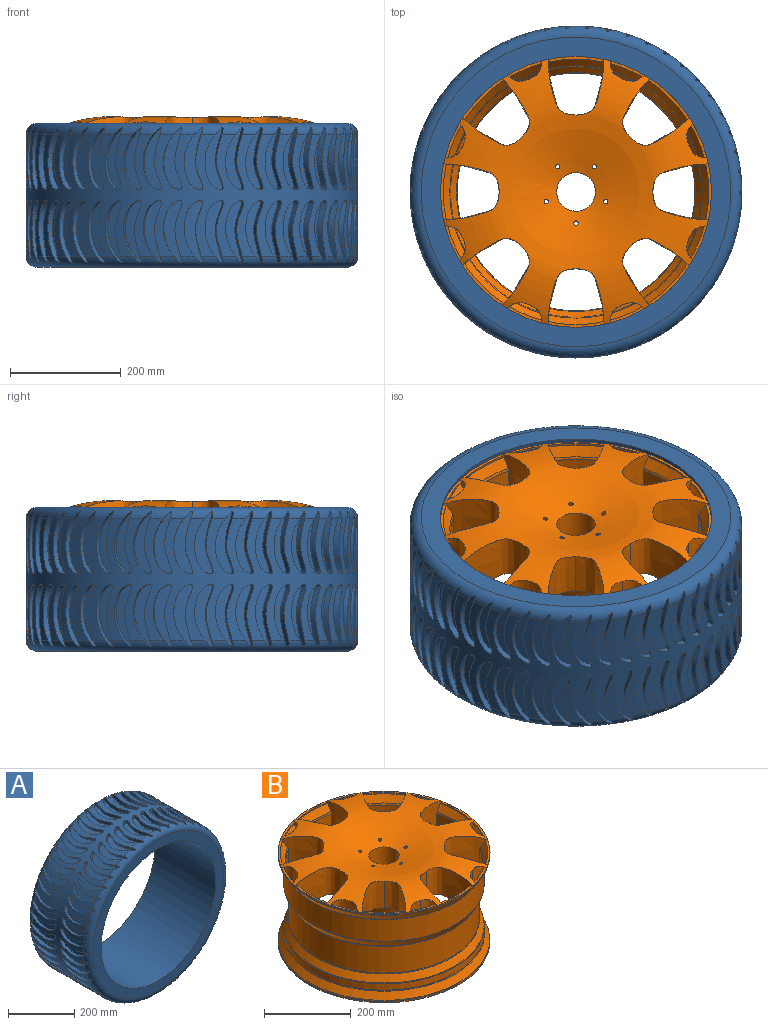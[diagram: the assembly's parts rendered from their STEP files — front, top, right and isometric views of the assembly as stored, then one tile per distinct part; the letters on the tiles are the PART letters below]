
ASSEMBLY  parts=2 mates=1
PART A: 208 faces, bbox 649.5x260x649.5 mm
  f0: cylinder r=300mm len=600mm, axis (0,1,0), area 178551.5mm2, adj f5,f7,f9,f11,f13,f15,f17,f19
  f1: plane 560x560mm, normal (0,1,0), area 57726.8mm2, adj f3,f206
  f2: plane 560x560mm, normal (0,-1,0), area 57726.8mm2, adj f3,f204
  f3: cylinder r=245mm len=490mm, axis (0,-1,0), area 400238.9mm2, adj f1,f2
  f4: plane 115.04x28.53mm, normal (0.64,0,0.77), area 2066.3mm2, adj f5
  f5: extruded ~112.28x33.37mm, area 2877.2mm2, adj f0,f4,f204
  f6: plane 115.04x35.82mm, normal (0.99,0,0.13), area 2066.3mm2, adj f7
  f7: extruded ~112.28x34.63mm, area 2877.2mm2, adj f0,f6,f204
  f8: plane 115.04x27.16mm, normal (0.73,0,-0.68), area 2066.3mm2, adj f9
  f9: extruded ~112.28x32.55mm, area 2877.2mm2, adj f0,f8,f204
  f10: plane 115.04x30.96mm, normal (0.54,0,-0.84), area 2066.3mm2, adj f11
  f11: extruded ~112.28x34.62mm, area 2877.2mm2, adj f0,f10,f204
  f12: plane 115.04x28.53mm, normal (0.64,0,-0.77), area 2066.3mm2, adj f13
  f13: extruded ~112.28x33.37mm, area 2877.2mm2, adj f0,f12,f204
  f14: plane 115.04x33.77mm, normal (0.93,0,-0.37), area 2066.3mm2, adj f15
  f15: extruded ~112.28x35.46mm, area 2877.2mm2, adj f0,f14,f204
  f16: plane 115.04x35.04mm, normal (0.97,0,-0.25), area 2066.3mm2, adj f17
  f17: extruded ~112.28x35.32mm, area 2877.2mm2, adj f0,f16,f204
  f18: plane 115.04x29.79mm, normal (0.81,0,-0.59), area 2066.3mm2, adj f19
  f19: extruded ~112.28x34.06mm, area 2877.2mm2, adj f0,f18,f204
  f20: plane 115.04x32.01mm, normal (0.88,0,-0.48), area 2066.3mm2, adj f21
  f21: extruded ~112.28x35.04mm, area 2877.2mm2, adj f0,f20,f204
  f22: plane 115.04x36.01mm, normal (0.06,0,-1), area 2066.3mm2, adj f23
  f23: extruded ~112.28x34.08mm, area 2877.2mm2, adj f0,f22,f204
  f24: plane 115.04x35.49mm, normal (0.19,0,-0.98), area 2066.3mm2, adj f25
  f25: extruded ~112.28x35.04mm, area 2877.2mm2, adj f0,f24,f204
  f26: plane 115.04x32.95mm, normal (0.43,0,-0.9), area 2066.3mm2, adj f27
  f27: extruded ~112.28x35.32mm, area 2877.2mm2, adj f0,f26,f204
  f28: plane 115.04x34.47mm, normal (0.31,0,-0.95), area 2066.3mm2, adj f29
  f29: extruded ~112.28x35.46mm, area 2877.2mm2, adj f0,f28,f204
  f30: plane 115.04x34.47mm, normal (-0.31,0,-0.95), area 2066.3mm2, adj f31
  f31: extruded ~112.28x35.46mm, area 2877.2mm2, adj f0,f30,f204
  f32: plane 115.04x32.95mm, normal (-0.43,0,-0.9), area 2066.3mm2, adj f33
  f33: extruded ~112.28x35.32mm, area 2877.2mm2, adj f0,f32,f204
  f34: plane 115.04x35.49mm, normal (-0.19,0,-0.98), area 2066.3mm2, adj f35
  f35: extruded ~112.28x35.04mm, area 2877.2mm2, adj f0,f34,f204
  f36: plane 115.04x36.01mm, normal (-0.06,0,-1), area 2066.3mm2, adj f37
  f37: extruded ~112.28x34.08mm, area 2877.2mm2, adj f0,f36,f204
  f38: plane 115.04x35.82mm, normal (0.99,0,-0.13), area 2066.3mm2, adj f39
  f39: extruded ~112.28x34.63mm, area 2877.2mm2, adj f0,f38,f204
  f40: plane 115.04x34.47mm, normal (-0.31,0,0.95), area 2066.3mm2, adj f41
  f41: extruded ~112.28x35.46mm, area 2877.2mm2, adj f0,f40,f204
  f42: plane 115.04x35.49mm, normal (-0.19,0,0.98), area 2066.3mm2, adj f43
  f43: extruded ~112.28x35.04mm, area 2877.2mm2, adj f0,f42,f204
  f44: plane 115.04x30.96mm, normal (-0.54,0,0.84), area 2066.3mm2, adj f45
  f45: extruded ~112.28x34.62mm, area 2877.2mm2, adj f0,f44,f204
  f46: plane 115.04x32.95mm, normal (-0.43,0,0.9), area 2066.3mm2, adj f47
  f47: extruded ~112.28x35.32mm, area 2877.2mm2, adj f0,f46,f204
  f48: plane 115.04x36.01mm, normal (-0.06,0,1), area 2066.3mm2, adj f49
  f49: extruded ~112.28x34.08mm, area 2877.2mm2, adj f0,f48,f204
  f50: plane 115.04x36.01mm, normal (0.06,0,1), area 2066.3mm2, adj f51
  f51: extruded ~112.28x34.08mm, area 2877.2mm2, adj f0,f50,f204
  f52: plane 115.04x34.47mm, normal (0.31,0,0.95), area 2066.3mm2, adj f53
  f53: extruded ~112.28x35.46mm, area 2877.2mm2, adj f0,f52,f204
  f54: plane 115.04x35.49mm, normal (0.19,0,0.98), area 2066.3mm2, adj f55
  f55: extruded ~112.28x35.04mm, area 2877.2mm2, adj f0,f54,f204
  f56: plane 115.04x27.16mm, normal (0.73,0,0.68), area 2066.3mm2, adj f57
  f57: extruded ~112.28x32.55mm, area 2877.2mm2, adj f0,f56,f204
  f58: plane 115.04x29.79mm, normal (0.81,0,0.59), area 2066.3mm2, adj f59
  f59: extruded ~112.28x34.06mm, area 2877.2mm2, adj f0,f58,f204
  f60: plane 115.04x30.96mm, normal (0.54,0,0.84), area 2066.3mm2, adj f61
  f61: extruded ~112.28x34.62mm, area 2877.2mm2, adj f0,f60,f204
  f62: plane 115.04x36.08mm, normal (1,0,0), area 2066.3mm2, adj f63
  f63: extruded ~112.28x33.39mm, area 2877.2mm2, adj f0,f62,f204
  f64: plane 115.04x32.95mm, normal (0.43,0,0.9), area 2066.3mm2, adj f65
  f65: extruded ~112.28x35.32mm, area 2877.2mm2, adj f0,f64,f204
  f66: plane 115.04x35.04mm, normal (0.97,0,0.25), area 2066.3mm2, adj f67
  f67: extruded ~112.28x35.32mm, area 2877.2mm2, adj f0,f66,f204
  f68: plane 115.04x32.01mm, normal (0.88,0,0.48), area 2066.3mm2, adj f69
  f69: extruded ~112.28x35.04mm, area 2877.2mm2, adj f0,f68,f204
  f70: plane 115.04x33.77mm, normal (0.93,0,0.37), area 2066.3mm2, adj f71
  f71: extruded ~112.28x35.46mm, area 2877.2mm2, adj f0,f70,f204
  f72: plane 115.04x35.04mm, normal (-0.97,0,0.25), area 2066.3mm2, adj f73
  f73: extruded ~112.28x35.32mm, area 2877.2mm2, adj f0,f72,f204
  f74: plane 115.04x33.77mm, normal (-0.93,0,0.37), area 2066.3mm2, adj f75
  f75: extruded ~112.28x35.46mm, area 2877.2mm2, adj f0,f74,f204
  f76: plane 115.04x35.82mm, normal (-0.99,0,0.13), area 2066.3mm2, adj f77
  f77: extruded ~112.28x34.63mm, area 2877.2mm2, adj f0,f76,f204
  f78: plane 115.04x36.08mm, normal (-1,0,0), area 2066.3mm2, adj f79
  f79: extruded ~112.28x33.39mm, area 2876.8mm2, adj f0,f78,f204,f205
  f80: plane 115.04x27.16mm, normal (-0.73,0,0.68), area 2066.3mm2, adj f81
  f81: extruded ~112.28x32.55mm, area 2877.2mm2, adj f0,f80,f204
  f82: plane 115.04x28.53mm, normal (-0.64,0,0.77), area 2066.3mm2, adj f83
  f83: extruded ~112.28x33.37mm, area 2877.2mm2, adj f0,f82,f204
  f84: plane 115.04x32.01mm, normal (-0.88,0,0.48), area 2066.3mm2, adj f85
  f85: extruded ~112.28x35.04mm, area 2877.2mm2, adj f0,f84,f204
  f86: plane 115.04x29.79mm, normal (-0.81,0,0.59), area 2066.3mm2, adj f87
  f87: extruded ~112.28x34.06mm, area 2877.2mm2, adj f0,f86,f204
  f88: plane 115.04x27.16mm, normal (-0.73,0,-0.68), area 2066.3mm2, adj f89
  f89: extruded ~112.28x32.55mm, area 2877.2mm2, adj f0,f88,f204
  f90: plane 115.04x29.79mm, normal (-0.81,0,-0.59), area 2066.3mm2, adj f91
  f91: extruded ~112.28x34.06mm, area 2877.2mm2, adj f0,f90,f204
  f92: plane 115.04x30.96mm, normal (-0.54,0,-0.84), area 2066.3mm2, adj f93
  f93: extruded ~112.28x34.62mm, area 2877.2mm2, adj f0,f92,f204
  f94: plane 115.04x28.53mm, normal (-0.64,0,-0.77), area 2066.3mm2, adj f95
  f95: extruded ~112.28x33.37mm, area 2877.2mm2, adj f0,f94,f204
  f96: plane 115.04x35.04mm, normal (-0.97,0,-0.25), area 2066.3mm2, adj f97
  f97: extruded ~112.28x35.32mm, area 2877.2mm2, adj f0,f96,f204
  f98: plane 115.04x35.82mm, normal (-0.99,0,-0.13), area 2066.3mm2, adj f99
  f99: extruded ~112.28x34.63mm, area 2877.2mm2, adj f0,f98,f204
  f100: plane 115.04x32.01mm, normal (-0.88,0,-0.48), area 2066.3mm2, adj f101
  f101: extruded ~112.28x35.04mm, area 2877.2mm2, adj f0,f100,f204
  f102: plane 115.04x33.77mm, normal (-0.93,0,-0.37), area 2066.3mm2, adj f103
  f103: extruded ~112.28x35.46mm, area 2877.2mm2, adj f0,f102,f204
  f104: plane 115.04x28.53mm, normal (0.64,0,0.77), area 2066.4mm2, adj f105
  f105: extruded ~112.28x33.37mm, area 2877.2mm2, adj f0,f104,f206
  f106: plane 115.04x35.5mm, normal (0.19,0,-0.98), area 2066.4mm2, adj f107
  f107: extruded ~112.28x35.04mm, area 2877.2mm2, adj f0,f106,f206
  f108: plane 115.04x34.47mm, normal (0.31,0,-0.95), area 2066.4mm2, adj f109
  f109: extruded ~112.28x35.46mm, area 2877.2mm2, adj f0,f108,f206
  f110: plane 115.04x30.96mm, normal (0.54,0,-0.84), area 2066.4mm2, adj f111
  f111: extruded ~112.28x34.62mm, area 2877.2mm2, adj f0,f110,f206
  f112: plane 115.04x35.04mm, normal (0.97,0,-0.25), area 2066.4mm2, adj f113
  f113: extruded ~112.28x35.32mm, area 2877.2mm2, adj f0,f112,f206
  f114: plane 115.04x35.04mm, normal (0.97,0,0.25), area 2066.4mm2, adj f115
  f115: extruded ~112.28x35.32mm, area 2877.2mm2, adj f0,f114,f206
  f116: plane 115.04x33.77mm, normal (0.93,0,-0.37), area 2066.4mm2, adj f117
  f117: extruded ~112.28x35.46mm, area 2877.2mm2, adj f0,f116,f206
  f118: plane 115.04x35.82mm, normal (0.99,0,-0.13), area 2066.4mm2, adj f119
  f119: extruded ~112.28x34.63mm, area 2877.2mm2, adj f0,f118,f206
  f120: plane 115.04x32.95mm, normal (0.43,0,-0.9), area 2066.4mm2, adj f121
  f121: extruded ~112.28x35.32mm, area 2877.2mm2, adj f0,f120,f206
  f122: plane 115.04x28.53mm, normal (0.64,0,-0.77), area 2066.4mm2, adj f123
  f123: extruded ~112.28x33.37mm, area 2877.2mm2, adj f0,f122,f206
  f124: plane 115.04x28.53mm, normal (-0.64,0,-0.77), area 2066.4mm2, adj f125
  f125: extruded ~112.28x33.37mm, area 2877.2mm2, adj f0,f124,f206
  f126: plane 115.04x32.95mm, normal (-0.43,0,-0.9), area 2066.4mm2, adj f127
  f127: extruded ~112.28x35.32mm, area 2877.2mm2, adj f0,f126,f206
  f128: plane 115.04x30.96mm, normal (-0.54,0,-0.84), area 2066.4mm2, adj f129
  f129: extruded ~112.28x34.62mm, area 2877.2mm2, adj f0,f128,f206
  f130: plane 115.04x36.08mm, normal (1,0,0), area 2066.4mm2, adj f131
  f131: extruded ~112.28x33.39mm, area 2877.2mm2, adj f0,f130,f206
  f132: plane 115.04x32.01mm, normal (0.88,0,-0.48), area 2066.4mm2, adj f133
  f133: extruded ~112.28x35.04mm, area 2877.2mm2, adj f0,f132,f206
  f134: plane 115.04x27.16mm, normal (0.73,0,-0.68), area 2066.4mm2, adj f135
  f135: extruded ~112.28x32.55mm, area 2877.2mm2, adj f0,f134,f206
  f136: plane 115.04x29.8mm, normal (0.81,0,-0.59), area 2066.4mm2, adj f137
  f137: extruded ~112.28x34.06mm, area 2877.2mm2, adj f0,f136,f206
  f138: plane 115.04x35.82mm, normal (0.99,0,0.13), area 2066.4mm2, adj f139
  f139: extruded ~112.28x34.63mm, area 2877.2mm2, adj f0,f138,f206
  f140: plane 115.04x30.96mm, normal (-0.54,0,0.84), area 2066.4mm2, adj f141
  f141: extruded ~112.28x34.62mm, area 2877.2mm2, adj f0,f140,f206
  f142: plane 115.04x32.95mm, normal (-0.43,0,0.9), area 2066.4mm2, adj f143
  f143: extruded ~112.28x35.32mm, area 2877.2mm2, adj f0,f142,f206
  f144: plane 115.04x27.16mm, normal (-0.73,0,0.68), area 2066.4mm2, adj f145
  f145: extruded ~112.28x32.55mm, area 2877.2mm2, adj f0,f144,f206
  f146: plane 115.04x28.53mm, normal (-0.64,0,0.77), area 2066.4mm2, adj f147
  f147: extruded ~112.28x33.37mm, area 2877.2mm2, adj f0,f146,f206
  f148: plane 115.04x36.01mm, normal (0.06,0,1), area 2066.4mm2, adj f149
  f149: extruded ~112.28x34.08mm, area 2877.2mm2, adj f0,f148,f206
  f150: plane 115.04x35.5mm, normal (0.19,0,0.98), area 2066.4mm2, adj f151
  f151: extruded ~112.28x35.04mm, area 2877.2mm2, adj f0,f150,f206
  f152: plane 115.04x32.95mm, normal (0.43,0,0.9), area 2066.4mm2, adj f153
  f153: extruded ~112.28x35.32mm, area 2877.2mm2, adj f0,f152,f206
  f154: plane 115.04x34.47mm, normal (0.31,0,0.95), area 2066.4mm2, adj f155
  f155: extruded ~112.28x35.46mm, area 2877.2mm2, adj f0,f154,f206
  f156: plane 115.04x29.8mm, normal (0.81,0,0.59), area 2066.4mm2, adj f157
  f157: extruded ~112.28x34.06mm, area 2877.2mm2, adj f0,f156,f206
  f158: plane 115.04x32.01mm, normal (0.88,0,0.48), area 2066.4mm2, adj f159
  f159: extruded ~112.28x35.04mm, area 2877.2mm2, adj f0,f158,f206
  f160: plane 115.04x27.16mm, normal (0.73,0,0.68), area 2066.4mm2, adj f161
  f161: extruded ~112.28x32.55mm, area 2877.2mm2, adj f0,f160,f206
  f162: plane 115.04x30.96mm, normal (0.54,0,0.84), area 2066.4mm2, adj f163
  f163: extruded ~112.28x34.62mm, area 2877.2mm2, adj f0,f162,f206
  f164: plane 115.04x36.01mm, normal (-0.06,0,1), area 2066.4mm2, adj f165
  f165: extruded ~112.28x34.08mm, area 2877.2mm2, adj f0,f164,f206
  f166: plane 115.04x35.5mm, normal (-0.19,0,0.98), area 2066.4mm2, adj f167
  f167: extruded ~112.28x35.04mm, area 2877.2mm2, adj f0,f166,f206
  f168: plane 115.04x34.47mm, normal (-0.31,0,0.95), area 2066.4mm2, adj f169
  f169: extruded ~112.28x35.46mm, area 2877.2mm2, adj f0,f168,f206
  f170: plane 115.04x33.77mm, normal (0.93,0,0.37), area 2066.4mm2, adj f171
  f171: extruded ~112.28x35.46mm, area 2877.2mm2, adj f0,f170,f206
  f172: plane 115.04x35.5mm, normal (-0.19,0,-0.98), area 2066.4mm2, adj f173
  f173: extruded ~112.28x35.04mm, area 2877.2mm2, adj f0,f172,f206
  f174: plane 115.04x34.47mm, normal (-0.31,0,-0.95), area 2066.4mm2, adj f175
  f175: extruded ~112.28x35.46mm, area 2877.2mm2, adj f0,f174,f206
  f176: plane 115.04x36.01mm, normal (-0.06,0,-1), area 2066.4mm2, adj f177
  f177: extruded ~112.28x34.08mm, area 2877.2mm2, adj f0,f176,f206
  f178: plane 115.04x36.01mm, normal (0.06,0,-1), area 2066.4mm2, adj f179
  f179: extruded ~112.28x34.08mm, area 2877.2mm2, adj f0,f178,f206
  f180: plane 115.04x32.01mm, normal (-0.88,0,-0.48), area 2066.4mm2, adj f181
  f181: extruded ~112.28x35.04mm, area 2877.2mm2, adj f0,f180,f206
  f182: plane 115.04x33.77mm, normal (-0.93,0,-0.37), area 2066.4mm2, adj f183
  f183: extruded ~112.28x35.46mm, area 2877.2mm2, adj f0,f182,f206
  f184: plane 115.04x27.16mm, normal (-0.73,0,-0.68), area 2066.4mm2, adj f185
  f185: extruded ~112.28x32.55mm, area 2877.2mm2, adj f0,f184,f206
  f186: plane 115.04x29.8mm, normal (-0.81,0,-0.59), area 2066.4mm2, adj f187
  f187: extruded ~112.28x34.06mm, area 2877.2mm2, adj f0,f186,f206
  f188: plane 115.04x33.77mm, normal (-0.93,0,0.37), area 2066.4mm2, adj f189
  f189: extruded ~112.28x35.46mm, area 2877.2mm2, adj f0,f188,f206
  f190: plane 115.04x35.04mm, normal (-0.97,0,0.25), area 2066.4mm2, adj f191
  f191: extruded ~112.28x35.32mm, area 2877.2mm2, adj f0,f190,f206
  f192: plane 115.04x29.8mm, normal (-0.81,0,0.59), area 2066.4mm2, adj f193
  f193: extruded ~112.28x34.06mm, area 2877.2mm2, adj f0,f192,f206
  f194: plane 115.04x32.01mm, normal (-0.88,0,0.48), area 2066.4mm2, adj f195
  f195: extruded ~112.28x35.04mm, area 2877.2mm2, adj f0,f194,f206
  f196: plane 115.04x35.82mm, normal (-0.99,0,0.13), area 2066.4mm2, adj f197
  f197: extruded ~112.28x34.63mm, area 2877.2mm2, adj f0,f196,f206
  f198: plane 115.04x36.08mm, normal (-1,0,0), area 2066.4mm2, adj f199
  f199: extruded ~112.28x33.39mm, area 2876.8mm2, adj f0,f198,f206,f207
  f200: plane 115.04x35.04mm, normal (-0.97,0,-0.25), area 2066.4mm2, adj f201
  f201: extruded ~112.28x35.32mm, area 2877.2mm2, adj f0,f200,f206
  f202: plane 115.04x35.82mm, normal (-0.99,0,-0.13), area 2066.4mm2, adj f203
  f203: extruded ~112.28x34.63mm, area 2877.2mm2, adj f0,f202,f206
  f204: torus R=280mm, axis (0,1,0), area 52595.4mm2, adj f0,f2,f5,f7,f9,f11,f13,f15
  f205: torus R=280mm, axis (0,1,0), area 6.9mm2, adj f0,f79,f204
  f206: torus R=280mm, axis (0,1,0), area 52606.5mm2, adj f0,f1,f105,f107,f109,f111,f113,f115
  f207: torus R=280mm, axis (0,1,0), area 6.9mm2, adj f0,f199,f206
PART B: 133 faces, bbox 530.4x530.4x270.1 mm
  f0: cylinder r=4mm len=167.44mm, axis (0,0,-1), area 4178.2mm2, adj f4,f28
  f1: cylinder r=4mm len=167.44mm, axis (0,0,-1), area 4178.2mm2, adj f4,f28
  f2: cylinder r=4mm len=167.44mm, axis (0,0,-1), area 4178.2mm2, adj f4,f28
  f3: cylinder r=4mm len=167.44mm, axis (0,0,-1), area 4178.2mm2, adj f4,f28
  f4: revolved ~490x490mm, area 106451.8mm2, adj f0,f1,f2,f3,f5,f6,f7,f8
  f5: extruded ~95.98x33.16mm, area 2397mm2, adj f4,f22,f29,f45,f61,f62,f77,f92
  f6: extruded ~95.98x39.81mm, area 2397mm2, adj f4,f22,f30,f46,f61,f63,f78,f93
  f7: extruded ~107.05x105.12mm, area 9144.7mm2, adj f4,f22,f31,f47,f61,f64,f79,f94
  f8: extruded ~105.12x100.76mm, area 9144.7mm2, adj f4,f22,f32,f48,f61,f74,f89,f104
  f9: extruded ~105.12x100.76mm, area 9144.7mm2, adj f4,f22,f33,f49,f61,f67,f82,f97
  f10: extruded ~95.98x33.16mm, area 2397mm2, adj f4,f22,f34,f50,f61,f65,f80,f95
  f11: extruded ~95.98x39.81mm, area 2397mm2, adj f4,f22,f35,f51,f61,f66,f81,f96
  f12: extruded ~107.05x105.12mm, area 9144.7mm2, adj f4,f22,f36,f52,f61,f68,f83,f98
  f13: extruded ~105.12x100.76mm, area 9144.7mm2, adj f4,f22,f37,f53,f61,f70,f85,f100
  f14: extruded ~95.98x39.81mm, area 2397mm2, adj f4,f22,f38,f54,f61,f69,f84,f99
  f15: extruded ~107.05x105.12mm, area 9144.7mm2, adj f4,f22,f39,f55,f61,f76,f91,f106
  f16: extruded ~107.05x105.12mm, area 9144.7mm2, adj f4,f22,f40,f56,f61,f72,f87,f102
  f17: extruded ~95.98x39.81mm, area 2397mm2, adj f4,f22,f41,f57,f61,f71,f86,f101
  f18: extruded ~95.98x33.16mm, area 2397mm2, adj f4,f22,f42,f58,f61,f73,f88,f103
  f19: extruded ~95.98x33.16mm, area 2397mm2, adj f4,f22,f43,f59,f61,f75,f90,f105
  f20: extruded ~105.12x100.76mm, area 9144.7mm2, adj f4,f22,f44,f60,f61,f113,f114,f119
  f21: cylinder r=245mm len=490mm, axis (0,0,-1), area 5871.6mm2, adj f4,f27,f45,f46,f47,f48,f49,f50
  f22: revolved ~454x454mm, area 130293mm2, adj f5,f6,f7,f8,f9,f10,f11,f12
  f23: torus R=228mm, axis (0,0,-1), area 3148.5mm2, adj f24,f124
  f24: cylinder r=232mm len=464mm, axis (0,0,-1), area 89949.2mm2, adj f23,f25
  f25: torus R=236mm, axis (0,0,-1), area 3363.9mm2, adj f24,f26
  f26: cone r=244.35mm half-angle=33deg, axis (0,0,1), area 32191.9mm2, adj f25,f27
  f27: torus R=241mm, axis (0,0,-1), area 3545.9mm2, adj f21,f26
  f28: plane 148.24x148.24mm, normal (0,0,-1), area 13159.5mm2, adj f0,f1,f2,f3,f22,f131,f132
  f29: extruded ~95.98x39.81mm, area 2397mm2, adj f4,f5,f22,f45,f61,f62,f77,f92
  f30: extruded ~95.98x33.16mm, area 2397mm2, adj f4,f6,f22,f46,f61,f63,f78,f93
  f31: extruded ~107.05x105.12mm, area 9144.7mm2, adj f4,f7,f22,f47,f61,f64,f79,f94
  f32: extruded ~105.12x100.76mm, area 9144.7mm2, adj f4,f8,f22,f48,f61,f74,f89,f104
  f33: extruded ~105.12x100.76mm, area 9144.7mm2, adj f4,f9,f22,f49,f61,f67,f82,f97
  f34: extruded ~95.98x39.81mm, area 2397mm2, adj f4,f10,f22,f50,f61,f65,f80,f95
  f35: extruded ~95.98x33.16mm, area 2397mm2, adj f4,f11,f22,f51,f61,f66,f81,f96
  f36: extruded ~107.05x105.12mm, area 9144.7mm2, adj f4,f12,f22,f52,f61,f68,f83,f98
  f37: extruded ~105.12x100.76mm, area 9144.7mm2, adj f4,f13,f22,f53,f61,f70,f85,f100
  f38: extruded ~95.98x33.16mm, area 2397mm2, adj f4,f14,f22,f54,f61,f69,f84,f99
  f39: extruded ~107.05x105.12mm, area 9144.7mm2, adj f4,f15,f22,f55,f61,f76,f91,f106
  f40: extruded ~107.05x105.12mm, area 9144.7mm2, adj f4,f16,f22,f56,f61,f72,f87,f102
  f41: extruded ~95.98x33.16mm, area 2397mm2, adj f4,f17,f22,f57,f61,f71,f86,f101
  f42: extruded ~95.98x39.81mm, area 2397mm2, adj f4,f18,f22,f58,f61,f73,f88,f103
  f43: extruded ~95.98x39.81mm, area 2397mm2, adj f4,f19,f22,f59,f61,f75,f90,f105
  f44: extruded ~105.12x100.76mm, area 9144.7mm2, adj f4,f20,f22,f60,f61,f113,f114,f119
  f45: plane 62.96x29.54mm, normal (0,0,1), area 330mm2, adj f5,f21,f29,f77
  f46: plane 62.96x29.54mm, normal (0,0,1), area 330mm2, adj f6,f21,f30,f78
  f47: plane 75.03x75.03mm, normal (0,0,1), area 508.9mm2, adj f7,f21,f31,f79
  f48: plane 101.25x10.36mm, normal (0,0,1), area 508.9mm2, adj f8,f21,f32,f89
  f49: plane 101.25x10.36mm, normal (0,0,1), area 508.9mm2, adj f9,f21,f33,f82
  f50: plane 62.96x29.54mm, normal (0,0,1), area 330mm2, adj f10,f21,f34,f80
  f51: plane 62.96x29.54mm, normal (0,0,1), area 330mm2, adj f11,f21,f35,f81
  f52: plane 75.03x75.03mm, normal (0,0,1), area 508.9mm2, adj f12,f21,f36,f83
  f53: plane 101.25x10.36mm, normal (0,0,1), area 508.9mm2, adj f13,f21,f37,f85
  f54: plane 62.96x29.54mm, normal (0,0,1), area 330mm2, adj f14,f21,f38,f84
  f55: plane 75.03x75.03mm, normal (0,0,1), area 508.9mm2, adj f15,f21,f39,f91
  f56: plane 75.03x75.03mm, normal (0,0,1), area 508.9mm2, adj f16,f21,f40,f87
  f57: plane 62.96x29.54mm, normal (0,0,1), area 330mm2, adj f17,f21,f41,f86
  f58: plane 62.96x29.54mm, normal (0,0,1), area 330mm2, adj f18,f21,f42,f88
  f59: plane 62.96x29.54mm, normal (0,0,1), area 330mm2, adj f19,f21,f43,f90
  f60: plane 101.25x10.36mm, normal (0,0,1), area 508.9mm2, adj f20,f21,f44,f114
  f61: cylinder r=227mm len=454mm, axis (0,0,1), area 70647.6mm2, adj f5,f6,f7,f8,f9,f10,f11,f12
  f62: cone r=227.81mm half-angle=33deg, axis (0,0,1), area 1167.8mm2, adj f5,f29,f77,f92
  f63: cone r=227.81mm half-angle=33deg, axis (0,0,1), area 1167.8mm2, adj f6,f30,f78,f93
  f64: cone r=227.81mm half-angle=33deg, axis (0,0,1), area 2137.5mm2, adj f7,f31,f79,f94
  f65: cone r=227.81mm half-angle=33deg, axis (0,0,1), area 1167.8mm2, adj f10,f34,f80,f95
  f66: cone r=227.81mm half-angle=33deg, axis (0,0,1), area 1167.8mm2, adj f11,f35,f81,f96
  f67: cone r=227.81mm half-angle=33deg, axis (0,0,1), area 2137.5mm2, adj f9,f33,f82,f97
  f68: cone r=227.81mm half-angle=33deg, axis (0,0,1), area 2137.5mm2, adj f12,f36,f83,f98
  f69: cone r=227.81mm half-angle=33deg, axis (0,0,1), area 1167.8mm2, adj f14,f38,f84,f99
  f70: cone r=227.81mm half-angle=33deg, axis (0,0,1), area 2137.5mm2, adj f13,f37,f85,f100
  f71: cone r=227.81mm half-angle=33deg, axis (0,0,1), area 1167.8mm2, adj f17,f41,f86,f101
  f72: cone r=227.81mm half-angle=33deg, axis (0,0,1), area 2137.5mm2, adj f16,f40,f87,f102
  f73: cone r=227.81mm half-angle=33deg, axis (0,0,1), area 1167.8mm2, adj f18,f42,f88,f103
  f74: cone r=227.81mm half-angle=33deg, axis (0,0,1), area 2137.5mm2, adj f8,f32,f89,f104
  f75: cone r=227.81mm half-angle=33deg, axis (0,0,1), area 1167.8mm2, adj f19,f43,f90,f105
  f76: cone r=227.81mm half-angle=33deg, axis (0,0,1), area 2137.5mm2, adj f15,f39,f91,f106
  f77: cylinder r=240mm len=58.53mm, axis (0,0,1), area 223.5mm2, adj f5,f29,f45,f62
  f78: cylinder r=240mm len=58.53mm, axis (0,0,1), area 223.5mm2, adj f6,f30,f46,f63
  f79: cylinder r=240mm len=71.29mm, axis (0,0,1), area 357.3mm2, adj f7,f31,f47,f64
  f80: cylinder r=240mm len=58.53mm, axis (0,0,1), area 223.5mm2, adj f10,f34,f50,f65
  f81: cylinder r=240mm len=58.53mm, axis (0,0,1), area 223.5mm2, adj f11,f35,f51,f66
  f82: cylinder r=240mm len=100.82mm, axis (0,0,1), area 357.3mm2, adj f9,f33,f49,f67
  f83: cylinder r=240mm len=71.29mm, axis (0,0,1), area 357.3mm2, adj f12,f36,f52,f68
  f84: cylinder r=240mm len=58.53mm, axis (0,0,1), area 223.5mm2, adj f14,f38,f54,f69
  f85: cylinder r=240mm len=100.82mm, axis (0,0,1), area 357.3mm2, adj f13,f37,f53,f70
  f86: cylinder r=240mm len=58.53mm, axis (0,0,1), area 223.5mm2, adj f17,f41,f57,f71
  f87: cylinder r=240mm len=71.29mm, axis (0,0,1), area 357.3mm2, adj f16,f40,f56,f72
  f88: cylinder r=240mm len=58.53mm, axis (0,0,1), area 223.5mm2, adj f18,f42,f58,f73
  f89: cylinder r=240mm len=100.82mm, axis (0,0,1), area 357.3mm2, adj f8,f32,f48,f74
  f90: cylinder r=240mm len=58.53mm, axis (0,0,1), area 223.5mm2, adj f19,f43,f59,f75
  f91: cylinder r=240mm len=71.29mm, axis (0,0,1), area 357.3mm2, adj f15,f39,f55,f76
  f92: torus R=236mm, axis (0,0,-1), area 234.3mm2, adj f5,f29,f61,f62
  f93: torus R=236mm, axis (0,0,-1), area 234.3mm2, adj f6,f30,f61,f63
  f94: torus R=236mm, axis (0,0,-1), area 518.4mm2, adj f7,f31,f61,f64
  f95: torus R=236mm, axis (0,0,-1), area 234.3mm2, adj f10,f34,f61,f65
  f96: torus R=236mm, axis (0,0,-1), area 234.3mm2, adj f11,f35,f61,f66
  f97: torus R=236mm, axis (0,0,-1), area 518.4mm2, adj f9,f33,f61,f67
  f98: torus R=236mm, axis (0,0,-1), area 518.4mm2, adj f12,f36,f61,f68
  f99: torus R=236mm, axis (0,0,-1), area 234.3mm2, adj f14,f38,f61,f69
  f100: torus R=236mm, axis (0,0,-1), area 518.4mm2, adj f13,f37,f61,f70
  f101: torus R=236mm, axis (0,0,-1), area 234.3mm2, adj f17,f41,f61,f71
  f102: torus R=236mm, axis (0,0,-1), area 518.4mm2, adj f16,f40,f61,f72
  f103: torus R=236mm, axis (0,0,-1), area 234.3mm2, adj f18,f42,f61,f73
  f104: torus R=236mm, axis (0,0,-1), area 518.4mm2, adj f8,f32,f61,f74
  f105: torus R=236mm, axis (0,0,-1), area 234.3mm2, adj f19,f43,f61,f75
  f106: torus R=236mm, axis (0,0,-1), area 518.4mm2, adj f15,f39,f61,f76
  f107: plane 490x490mm, normal (0,0,-1), area 7618.4mm2, adj f115,f125
  f108: cone r=240.81mm half-angle=33deg, axis (0,0,-1), area 31178.9mm2, adj f115,f116
  f109: cylinder r=227mm len=454mm, axis (0,0,1), area 24859.1mm2, adj f110,f116
  f110: cone r=227.71mm half-angle=31deg, axis (0,0,-1), area 29009.5mm2, adj f109,f117
  f111: cylinder r=215mm len=430mm, axis (0,0,1), area 102375.6mm2, adj f117,f118
  f112: cone r=215.71mm half-angle=31deg, axis (0,0,1), area 29009.5mm2, adj f61,f118
  f113: cone r=227.81mm half-angle=33deg, axis (0,0,1), area 2137.5mm2, adj f20,f44,f114,f119
  f114: cylinder r=240mm len=100.82mm, axis (0,0,1), area 357.3mm2, adj f20,f44,f60,f113
  f115: cylinder r=240mm len=480mm, axis (0,0,1), area 5304.7mm2, adj f107,f108
  f116: torus R=236mm, axis (0,0,-1), area 7414.6mm2, adj f108,f109
  f117: torus R=224mm, axis (0,0,-1), area 6583.6mm2, adj f110,f111
  f118: torus R=224mm, axis (0,0,-1), area 6583.6mm2, adj f111,f112
  f119: torus R=236mm, axis (0,0,-1), area 518.4mm2, adj f20,f44,f61,f113
  f120: cone r=245mm half-angle=33deg, axis (0,0,-1), area 32191.9mm2, adj f126,f127
  f121: cylinder r=232mm len=464mm, axis (0,0,1), area 25810.5mm2, adj f127,f128
  f122: cone r=232mm half-angle=31deg, axis (0,0,-1), area 29973.3mm2, adj f128,f129
  f123: cylinder r=220mm len=440mm, axis (0,0,1), area 104756.5mm2, adj f129,f130
  f124: cone r=220mm half-angle=31deg, axis (0,0,1), area 29973.3mm2, adj f23,f130
  f125: cylinder r=245mm len=490mm, axis (0,0,1), area 5871.6mm2, adj f107,f126
  f126: torus R=241mm, axis (0,0,1), area 3545.9mm2, adj f120,f125
  f127: torus R=236mm, axis (0,0,-1), area 3363.9mm2, adj f120,f121
  f128: torus R=228mm, axis (0,0,1), area 3148.5mm2, adj f121,f122
  f129: torus R=224mm, axis (0,0,-1), area 2990.7mm2, adj f122,f123
  f130: torus R=224mm, axis (0,0,-1), area 2990.7mm2, adj f123,f124
  f131: cylinder r=35mm len=160.41mm, axis (0,0,-1), area 35275.5mm2, adj f4,f28
  f132: cylinder r=4mm len=167.44mm, axis (0,0,-1), area 4178.2mm2, adj f4,f28
PLACE A rot(axis=(1,0,0),90deg) t=(-887.65,-485.48,5.89)mm
PLACE B t=(-887.65,-485.48,-105.26)mm
MATE slider B.f21 <-> A.f3  axis (0,0,1) through (-887.65,-485.48,-18.48)mm
